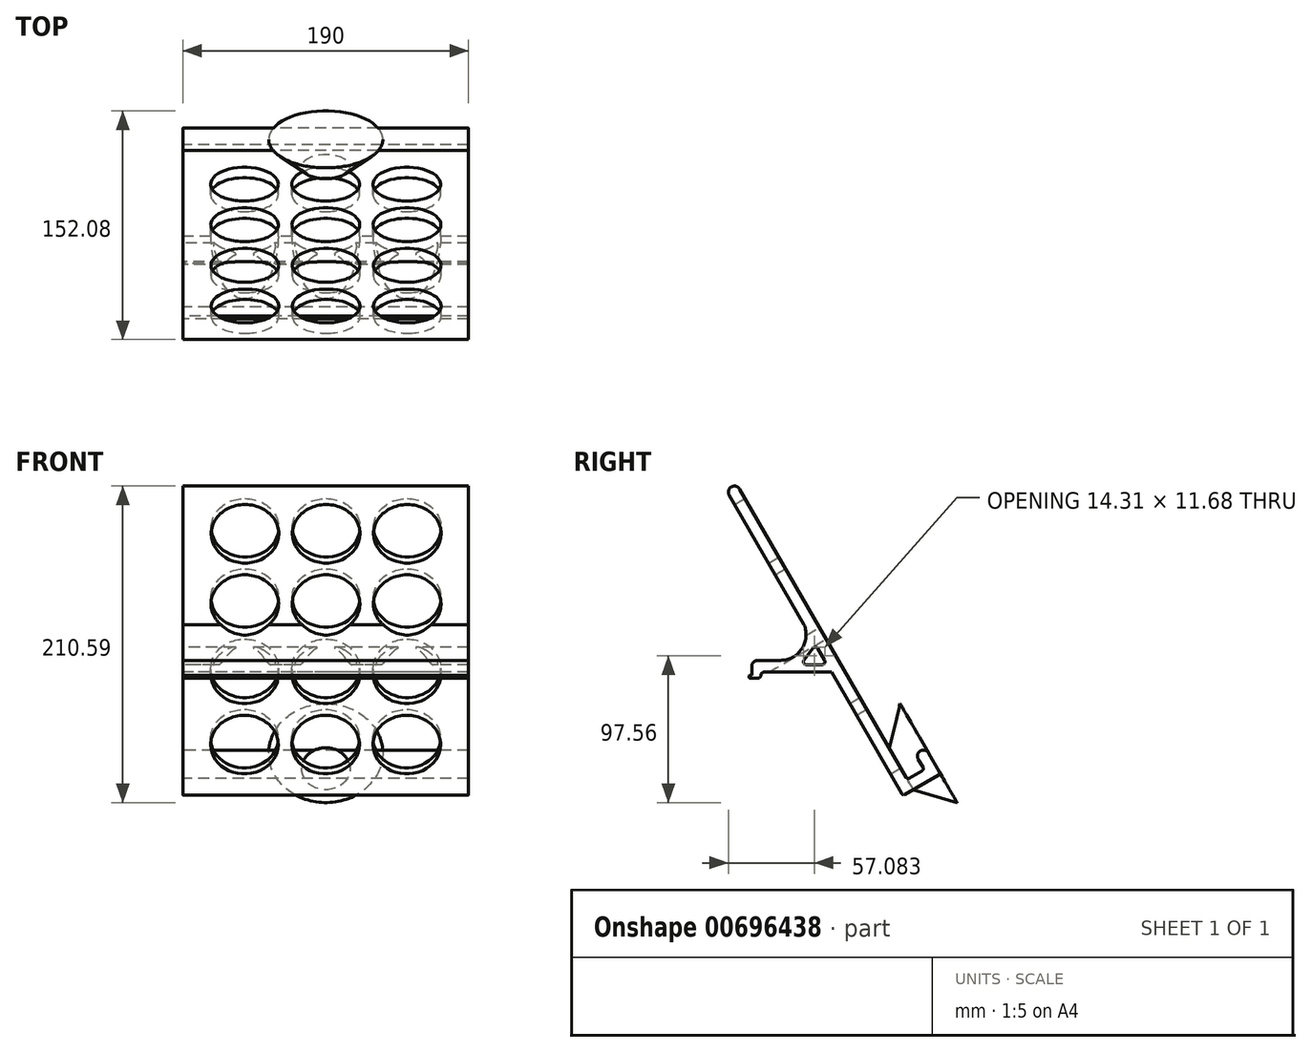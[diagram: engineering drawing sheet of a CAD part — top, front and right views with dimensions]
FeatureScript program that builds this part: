
annotation { "Feature Type Name" : "Feature", "Feature Type Description" : "" }
export const myFeature = defineFeature(function(context is Context, id is Id, definition is map)
    precondition{}
    {
        {
            var Q0;
            Q0=qCreatedBy(makeId("Right.planeOp"),FACE);
            var sketch = newSketch(context, id + "F0", { "sketchPlane" : qUnion([Q0])});
            skLineSegment(sketch, "E0", {"start": v(-55.38, 95.91) * mm, "end": v(55.38, -95.91) * mm});
            skLineSegment(sketch, "E1", {"start": v(57.42, -96.46) * mm, "end": v(66.08, -91.46) * mm});
            skLineSegment(sketch, "E2", {"start": v(66.63, -89.41) * mm, "end": v(63.38, -83.78) * mm});
            skLineSegment(sketch, "E3", {"start": v(-74.67, 0) * mm, "end": v(75.15, 0) * mm, "construction": true});
            skLineSegment(sketch, "E4.0", {"start": v(77.56, -92.34) * mm, "end": v(70.31, -79.78) * mm});
            skLineSegment(sketch, "E4.1", {"start": v(54.5, -107.39) * mm, "end": v(77.01, -94.39) * mm});
            skLineSegment(sketch, "E4.2", {"start": v(-62.3, 91.91) * mm, "end": v(52.45, -106.84) * mm});
            skArc(sketch, "E5", {"start": v(70.31, -79.78) * mm, "mid": v(64.85, -78.32) * mm, "end": v(63.38, -83.78) * mm});
            skArc(sketch, "E6", {"start": v(-55.38, 95.91) * mm, "mid": v(-60.84, 97.38) * mm, "end": v(-62.3, 91.91) * mm});
            skLineSegment(sketch, "E7", {"start": v(5.75, -25.96) * mm, "end": v(-39.25, -25.96) * mm});
            skLineSegment(sketch, "E8", {"start": v(-41.25, -27.96) * mm, "end": v(-41.25, -27.96) * mm});
            skLineSegment(sketch, "E9", {"start": v(-43.25, -29.96) * mm, "end": v(-48.25, -29.96) * mm});
            skLineSegment(sketch, "E10", {"start": v(-49.25, -28.96) * mm, "end": v(-49.25, -28.96) * mm});
            skLineSegment(sketch, "E11", {"start": v(-48.25, -27.96) * mm, "end": v(-47.25, -27.96) * mm});
            skLineSegment(sketch, "E12", {"start": v(-47.25, -27.96) * mm, "end": v(-47.25, -25.96) * mm});
            skLineSegment(sketch, "E13", {"start": v(-47.25, -25.96) * mm, "end": v(-47.25, -22.05) * mm});
            skLineSegment(sketch, "E14", {"start": v(-43.25, -18.05) * mm, "end": v(-28.25, -18.05) * mm});
            skPoint(sketch, "E14.endSnap0", {"position": v(-17.75, -25.96) * mm});
            skPoint(sketch, "E15.visualSharp", {"position": v(-47.25, -13.5) * mm});
            skArc(sketch, "E15.filletArc", {"start": v(-43.25, -18.05) * mm, "mid": v(-46.08, -19.23) * mm, "end": v(-47.25, -22.05) * mm});
            skPoint(sketch, "E16.visualSharp", {"position": v(-41.25, -25.96) * mm});
            skArc(sketch, "E16.filletArc", {"start": v(-39.25, -25.96) * mm, "mid": v(-40.66, -26.55) * mm, "end": v(-41.25, -27.96) * mm});
            skPoint(sketch, "E17.visualSharp", {"position": v(-49.25, -27.96) * mm});
            skArc(sketch, "E17.filletArc", {"start": v(-48.25, -27.96) * mm, "mid": v(-48.96, -28.25) * mm, "end": v(-49.25, -28.96) * mm});
            skPoint(sketch, "E18.visualSharp", {"position": v(-49.25, -29.96) * mm});
            skArc(sketch, "E18.filletArc", {"start": v(-49.25, -28.96) * mm, "mid": v(-48.96, -29.67) * mm, "end": v(-48.25, -29.96) * mm});
            skPoint(sketch, "E19.visualSharp", {"position": v(-41.25, -29.96) * mm});
            skArc(sketch, "E20", {"start": v(-28.25, -18.05) * mm, "mid": v(-14.05, -10.47) * mm, "end": v(-12.44, 5.55) * mm});
            skPoint(sketch, "E21.visualSharp", {"position": v(78.31, -93.64) * mm});
            skArc(sketch, "E21.filletArc", {"start": v(77.01, -94.39) * mm, "mid": v(77.71, -93.48) * mm, "end": v(77.56, -92.34) * mm});
            skPoint(sketch, "E22.visualSharp", {"position": v(53.2, -108.14) * mm});
            skArc(sketch, "E22.filletArc", {"start": v(52.45, -106.84) * mm, "mid": v(53.36, -107.54) * mm, "end": v(54.5, -107.39) * mm});
            skPoint(sketch, "E23.visualSharp", {"position": v(56.13, -97.21) * mm});
            skArc(sketch, "E23.filletArc", {"start": v(55.38, -95.91) * mm, "mid": v(56.29, -96.61) * mm, "end": v(57.42, -96.46) * mm});
            skPoint(sketch, "E24.visualSharp", {"position": v(67.38, -90.71) * mm});
            skArc(sketch, "E24.filletArc", {"start": v(66.08, -91.46) * mm, "mid": v(66.78, -90.55) * mm, "end": v(66.63, -89.41) * mm});
            skArc(sketch, "E25", {"start": v(6.24, -26.81) * mm, "mid": v(5.54, -26.2) * mm, "end": v(4.62, -25.96) * mm});
            skLineSegment(sketch, "E26", {"start": v(-12.51, -17.74) * mm, "end": v(-6.62, -10.06) * mm});
            skLineSegment(sketch, "E27", {"start": v(-3.3, -10.28) * mm, "end": v(1.13, -17.96) * mm});
            skLineSegment(sketch, "E28", {"start": v(-0.6, -20.96) * mm, "end": v(-10.92, -20.96) * mm});
            skPoint(sketch, "E29.visualSharp", {"position": v(-4.8, -7.68) * mm});
            skArc(sketch, "E29.filletArc", {"start": v(-3.3, -10.28) * mm, "mid": v(-4.9, -9.28) * mm, "end": v(-6.62, -10.06) * mm});
            skArc(sketch, "E30.filletArc", {"start": v(-12.51, -17.74) * mm, "mid": v(-12.72, -19.85) * mm, "end": v(-10.92, -20.96) * mm});
            skPoint(sketch, "E31.visualSharp", {"position": v(2.86, -20.96) * mm});
            skArc(sketch, "E31.filletArc", {"start": v(-0.6, -20.96) * mm, "mid": v(1.13, -19.96) * mm, "end": v(1.13, -17.96) * mm});
            skArc(sketch, "E32.filletArc", {"start": v(-43.25, -29.96) * mm, "mid": v(-41.84, -29.37) * mm, "end": v(-41.25, -27.96) * mm});
            skSolve(sketch);
        }
        {
            var Q0;
            Q0=makeQuery(id+"F0.imprint","IMPRINT",FACE,{"disambiguationData":[TD([[makeQuery(id+"F0.imprint","IMPRINT",EDGE,{"derivedFrom":sQuery(id+"F0.wireOp",EDGE,"E9")}),-1.0]])]});
            var Q1;
            Q1=makeQuery(id+"F0.imprint","IMPRINT",FACE,{"disambiguationData":[TD([[makeQuery(id+"F0.imprint","IMPRINT",EDGE,{"derivedFrom":sQuery(id+"F0.wireOp",EDGE,"E0")}),-1.0]])]});
            extrude(context, id + "F1", {"entities" : qUnion([Q0, Q1]), "endBound" : BoundingType.SYMMETRIC, "depth" : 190 * mm, "offsetDistance" : 25 * mm});
        }
        {
            var Q0;
            Q0=makeQuery(id+"F607cGiYLZ7bgVW_1.boolean.opBoolean","MERGE",FACE,{"derivedFrom":[makeQuery(id+"F1.opExtrude","SWEPT_FACE",FACE,{"disambiguationData":[OSD([sQuery(id+"F0.wireOp",EDGE,"E0")])]}),makeQuery(id+"F607cGiYLZ7bgVW_1.opExtrude","CAP_FACE",FACE,{"disambiguationData":[OSD([sQuery(id+"FD3LpnMe8WBRvEz_1.wireOp",EDGE,"oLRLmjWs-WXyG-iy66-VNn9-g0rHoBBj1zmg")])],"isStart":true})]});
            var sketch = newSketch(context, id + "F2", { "sketchPlane" : qUnion([Q0])});
            skCircle(sketch, "E33", {"center": v(-54.28, 81) * mm, "radius": 22.5 * mm});
            skCircle(sketch, "E34.0.1.0", {"center": v(-54.15, 27) * mm, "radius": 22.5 * mm});
            skCircle(sketch, "E34.0.2.0", {"center": v(-54.02, -27) * mm, "radius": 22.5 * mm});
            skCircle(sketch, "E34.0.3.0", {"center": v(-53.89, -81) * mm, "radius": 22.5 * mm});
            skCircle(sketch, "E34.1.0.0", {"center": v(-0.28, 81) * mm, "radius": 22.5 * mm});
            skCircle(sketch, "E34.1.1.0", {"center": v(-0.15, 27) * mm, "radius": 22.5 * mm});
            skCircle(sketch, "E34.1.2.0", {"center": v(-0.02, -27) * mm, "radius": 22.5 * mm});
            skCircle(sketch, "E34.1.3.0", {"center": v(0.11, -81) * mm, "radius": 22.5 * mm});
            skCircle(sketch, "E34.2.0.0", {"center": v(53.72, 81) * mm, "radius": 22.5 * mm});
            skCircle(sketch, "E34.2.1.0", {"center": v(53.85, 27) * mm, "radius": 22.5 * mm});
            skCircle(sketch, "E34.2.2.0", {"center": v(53.98, -27) * mm, "radius": 22.5 * mm});
            skCircle(sketch, "E34.2.3.0", {"center": v(54.11, -81) * mm, "radius": 22.5 * mm});
            skLineSegment(sketch, "E34.direction1", {"start": v(-54.28, 81) * mm, "end": v(-0.28, 81) * mm, "construction": true});
            skLineSegment(sketch, "E34.direction2", {"start": v(-54.28, 81) * mm, "end": v(-54.15, 27) * mm, "construction": true});
            skLineSegment(sketch, "E35", {"start": v(-75.26, 0) * mm, "end": v(74.88, 0) * mm, "construction": true});
            skLineSegment(sketch, "E36.0", {"start": v(-75.26, -27) * mm, "end": v(74.88, -27) * mm, "construction": true});
            skSolve(sketch);
        }
        {
            var Q0;
            Q0 = qSketchRegion(id + "F2", true);
            extrude(context, id + "F3", {"entities" : qUnion([Q0]), "operationType" : NewBodyOperationType.REMOVE, "endBound" : BoundingType.UP_TO_NEXT, "oppositeDirection" : true, "depth" : 25 * mm, "offsetDistance" : 25 * mm});
        }
        {
            var Q0;
            Q0=qCreatedBy(makeId("Right.planeOp"),FACE);
            var sketch = newSketch(context, id + "F4", { "sketchPlane" : qUnion([Q0])});
            skLineSegment(sketch, "E37", {"start": v(70.31, -79.78) * mm, "end": v(52.17, -90.22) * mm});
            skLineSegment(sketch, "E38", {"start": v(44.13, -76.23) * mm, "end": v(51.38, -46.88) * mm});
            skLineSegment(sketch, "E39", {"start": v(51.38, -46.88) * mm, "end": v(70.31, -79.78) * mm});
            skLineSegment(sketch, "E40", {"start": v(44.13, -76.23) * mm, "end": v(52.17, -90.22) * mm});
            skLineSegment(sketch, "E41.0", {"start": v(70.31, -79.78) * mm, "end": v(51.38, -46.88) * mm, "construction": true});
            skSolve(sketch);
        }
        {
            var Q0;
            Q0=makeQuery(id+"F4.imprint","IMPRINT",FACE,{"disambiguationData":[TD([[makeQuery(id+"F4.imprint","IMPRINT",EDGE,{"derivedFrom":sQuery(id+"F4.wireOp",EDGE,"E37")}),-1.0]])]});
            var Q1;
            Q1=sQuery(id+"F4.wireOp",EDGE,"E37");
            revolve(context, id + "F5", {"entities" : qUnion([Q0]), "axis" : qUnion([Q1]), "revolveType" : RevolveType.FULL});
        }
    });
